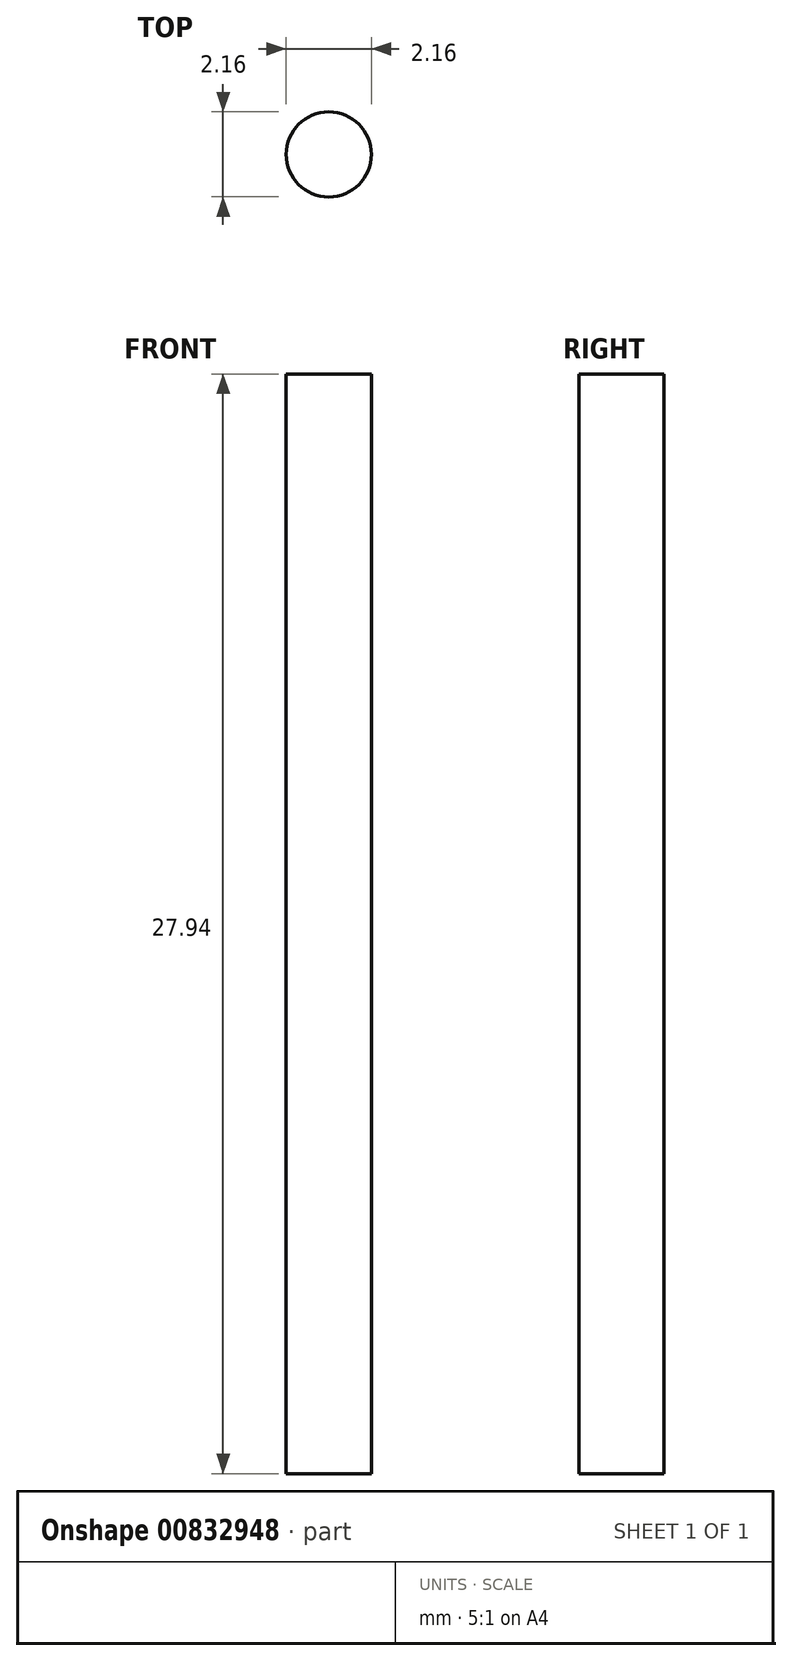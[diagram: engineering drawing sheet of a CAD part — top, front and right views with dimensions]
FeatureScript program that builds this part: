
annotation { "Feature Type Name" : "Feature", "Feature Type Description" : "" }
export const myFeature = defineFeature(function(context is Context, id is Id, definition is map)
    precondition{}
    {
        {
            var Q0;
            Q0=qCreatedBy(makeId("Top.planeOp"),FACE);
            var sketch = newSketch(context, id + "F0", { "sketchPlane" : qUnion([Q0])});
            skCircle(sketch, "E0", {"center": v(0, 0) * mm, "radius": 1.08 * mm});
            skSolve(sketch);
        }
        {
            var Q0;
            Q0 = qSketchRegion(id + "F0", true);
            extrude(context, id + "F1", {"entities" : qUnion([Q0]), "depth" : 27.94 * mm, "offsetDistance" : 25.4 * mm});
        }
    });
